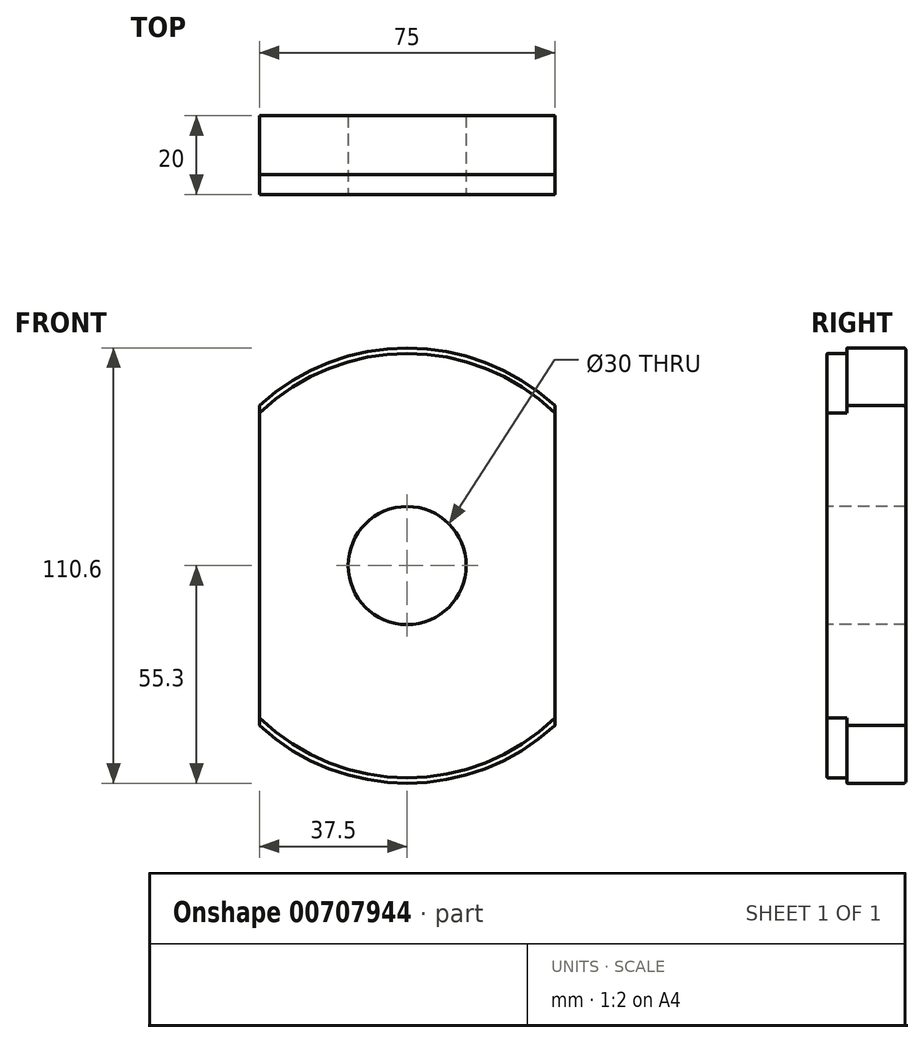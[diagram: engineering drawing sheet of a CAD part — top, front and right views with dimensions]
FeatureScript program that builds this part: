
annotation { "Feature Type Name" : "Feature", "Feature Type Description" : "" }
export const myFeature = defineFeature(function(context is Context, id is Id, definition is map)
    precondition{}
    {
        {
            var Q0;
            Q0=qCreatedBy(makeId("Front.planeOp"),FACE);
            var sketch = newSketch(context, id + "F0", { "sketchPlane" : qUnion([Q0])});
            skCircle(sketch, "E0", {"center": v(0, 0) * mm, "radius": 55.3 * mm});
            skSolve(sketch);
        }
        {
            var Q0;
            Q0=makeQuery(id+"F0.imprint","IMPRINT",FACE,{"disambiguationData":[TD([[makeQuery(id+"F0.imprint","IMPRINT",EDGE,{"derivedFrom":sQuery(id+"F0.wireOp",EDGE,"E0")}),1.0]])]});
            extrude(context, id + "F1", {"entities" : qUnion([Q0]), "depth" : 15 * mm, "offsetDistance" : 25 * mm});
        }
        {
            var Q0;
            Q0=makeQuery(id+"F1.opExtrude","CAP_FACE",FACE,{"disambiguationData":[OSD([sQuery(id+"F0.wireOp",EDGE,"E0")])],"isStart":false});
            var sketch = newSketch(context, id + "F2", { "sketchPlane" : qUnion([Q0])});
            skCircle(sketch, "E1", {"center": v(0, 0) * mm, "radius": 53.9 * mm});
            skSolve(sketch);
        }
        {
            var Q0;
            Q0=makeQuery(id+"F2.imprint","IMPRINT",FACE,{"disambiguationData":[TD([[makeQuery(id+"F2.imprint","IMPRINT",EDGE,{"derivedFrom":sQuery(id+"F2.wireOp",EDGE,"E1")}),1.0]])]});
            extrude(context, id + "F3", {"entities" : qUnion([Q0]), "operationType" : NewBodyOperationType.ADD, "depth" : 5 * mm, "offsetDistance" : 25 * mm});
        }
        {
            var Q0;
            Q0=makeQuery(id+"F3.opExtrude","CAP_FACE",FACE,{"disambiguationData":[OSD([sQuery(id+"F2.wireOp",EDGE,"E1")])],"isStart":false});
            var sketch = newSketch(context, id + "F4", { "sketchPlane" : qUnion([Q0])});
            skCircle(sketch, "E2", {"center": v(0, 0) * mm, "radius": 15 * mm});
            skSolve(sketch);
        }
        {
            var Q0;
            Q0=makeQuery(id+"F4.imprint","IMPRINT",FACE,{"disambiguationData":[TD([[makeQuery(id+"F4.imprint","IMPRINT",EDGE,{"derivedFrom":sQuery(id+"F4.wireOp",EDGE,"E2")}),1.0]])]});
            extrude(context, id + "F5", {"entities" : qUnion([Q0]), "operationType" : NewBodyOperationType.REMOVE, "oppositeDirection" : true, "depth" : 25 * mm, "offsetDistance" : 25 * mm});
        }
        {
            var Q0;
            Q0=makeQuery(id+"F1.opExtrude","CAP_FACE",FACE,{"disambiguationData":[OSD([sQuery(id+"F0.wireOp",EDGE,"E0")])],"isStart":true});
            var sketch = newSketch(context, id + "F6", { "sketchPlane" : qUnion([Q0])});
            skLineSegment(sketch, "E3.bottom", {"start": v(-37.5, -70.9) * mm, "end": v(37.5, -70.9) * mm});
            skLineSegment(sketch, "E3.top", {"start": v(-37.5, 70.9) * mm, "end": v(37.5, 70.9) * mm});
            skLineSegment(sketch, "E3.left", {"start": v(-37.5, -70.9) * mm, "end": v(-37.5, 70.9) * mm});
            skLineSegment(sketch, "E3.right", {"start": v(37.5, -70.9) * mm, "end": v(37.5, 70.9) * mm});
            skPoint(sketch, "E3.middle", {"position": v(0, 0) * mm});
            skSolve(sketch);
        }
        {
            var Q0;
            {var subQ0=sQuery(id+"F6.wireOp",EDGE,"E3.right");var subQ1=makeQuery(id+"F1.opExtrude","CAP_EDGE",EDGE,{"disambiguationData":[OSD([sQuery(id+"F0.wireOp",EDGE,"E0")])],"isStart":true});var subQ2=makeQuery(id+"F6.imprint","INTERSECT",VERTEX,{"disambiguationData":[OD(0.0)],"derivedFrom":[subQ1,subQ0]});Q0=makeQuery(id+"F6.imprint","IMPRINT",FACE,{"disambiguationData":[TD([[makeQuery(id+"F6.imprint","IMPRINT",EDGE,{"disambiguationData":[TD([[subQ2,-1.0]])],"derivedFrom":subQ0}),-1.0]])]});}
            var Q1;
            {var subQ0=sQuery(id+"F6.wireOp",EDGE,"E3.left");var subQ1=makeQuery(id+"F1.opExtrude","CAP_EDGE",EDGE,{"disambiguationData":[OSD([sQuery(id+"F0.wireOp",EDGE,"E0")])],"isStart":true});var subQ2=makeQuery(id+"F6.imprint","INTERSECT",VERTEX,{"disambiguationData":[OD(0.0)],"derivedFrom":[subQ1,subQ0]});Q1=makeQuery(id+"F6.imprint","IMPRINT",FACE,{"disambiguationData":[TD([[makeQuery(id+"F6.imprint","IMPRINT",EDGE,{"disambiguationData":[TD([[subQ2,-1.0]])],"derivedFrom":subQ0}),1.0]])]});}
            extrude(context, id + "F7", {"entities" : qUnion([Q0, Q1]), "operationType" : NewBodyOperationType.REMOVE, "oppositeDirection" : true, "depth" : 25 * mm, "offsetDistance" : 25 * mm});
        }
        {
            var Q0;
            Q0=makeQuery(id+"F7.boolean.opBoolean","COPY",EDGE,{"derivedFrom":makeQuery(id+"F7.opExtrude","CAP_EDGE",EDGE,{"disambiguationData":[OSD([sQuery(id+"F6.wireOp",EDGE,"E3.left")])],"isStart":true})});
            var Q1;
            Q1=makeQuery(id+"F7.boolean.opBoolean","SPLIT",EDGE,{"disambiguationData":[OD(0.0)],"derivedFrom":makeQuery(id+"F1.opExtrude","CAP_EDGE",EDGE,{"disambiguationData":[OSD([sQuery(id+"F0.wireOp",EDGE,"E0")])],"isStart":true})});
            var Q2;
            Q2=makeQuery(id+"F7.boolean.opBoolean","COPY",EDGE,{"derivedFrom":makeQuery(id+"F7.opExtrude","CAP_EDGE",EDGE,{"disambiguationData":[OSD([sQuery(id+"F6.wireOp",EDGE,"E3.right")])],"isStart":true})});
            var Q3;
            Q3=makeQuery(id+"F7.boolean.opBoolean","SPLIT",EDGE,{"disambiguationData":[OD(1.0)],"derivedFrom":makeQuery(id+"F1.opExtrude","CAP_EDGE",EDGE,{"disambiguationData":[OSD([sQuery(id+"F0.wireOp",EDGE,"E0")])],"isStart":true})});
            fillet(context, id + "F8", {"entities" : qUnion([Q0, Q1, Q2, Q3]), "radius" : 0.5 * mm, "tangentPropagation" : true, "allowEdgeOverflow" : false});
        }
        {
            var Q0;
            Q0=makeQuery(id+"F7.boolean.opBoolean","SPLIT",EDGE,{"disambiguationData":[OD(1.0)],"derivedFrom":makeQuery(id+"F3.opExtrude","CAP_EDGE",EDGE,{"disambiguationData":[OSD([sQuery(id+"F2.wireOp",EDGE,"E1")])],"isStart":false})});
            var Q1;
            Q1=makeQuery(id+"F7.boolean.opBoolean","SPLIT",EDGE,{"disambiguationData":[OD(1.0)],"derivedFrom":makeQuery(id+"F1.opExtrude","CAP_EDGE",EDGE,{"disambiguationData":[OSD([sQuery(id+"F0.wireOp",EDGE,"E0")])],"isStart":false})});
            var Q2;
            Q2=makeQuery(id+"F7.boolean.opBoolean","SPLIT",EDGE,{"disambiguationData":[OD(0.0)],"derivedFrom":makeQuery(id+"F3.opExtrude","CAP_EDGE",EDGE,{"disambiguationData":[OSD([sQuery(id+"F2.wireOp",EDGE,"E1")])],"isStart":false})});
            var Q3;
            Q3=makeQuery(id+"F7.boolean.opBoolean","SPLIT",EDGE,{"disambiguationData":[OD(0.0)],"derivedFrom":makeQuery(id+"F1.opExtrude","CAP_EDGE",EDGE,{"disambiguationData":[OSD([sQuery(id+"F0.wireOp",EDGE,"E0")])],"isStart":false})});
            fillet(context, id + "F9", {"entities" : qUnion([Q0, Q1, Q2, Q3]), "radius" : 0.2 * mm, "tangentPropagation" : true, "allowEdgeOverflow" : false});
        }
    });
